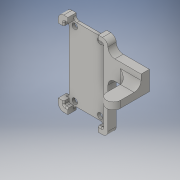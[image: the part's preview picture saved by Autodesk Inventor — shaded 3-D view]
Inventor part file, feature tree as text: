
AUTODESK INVENTOR PART (.ipt)
format: ipt  version: 2016 (Build 200138000, 138)  size: 251,392 bytes
history: native  units: in
note: dims shown in document units (in); Inventor stores cm internally (conversion verified against a paired STEP export)
features: fillet x5, extrude x4, sketch x3
ambient origin geometry x8: Origin, YZ Plane, XZ Plane, XY Plane, X Axis, Y Axis, Z Axis, Center Point
bodies: Solid1 (feature_tree)
feature tree (12):
  sketch  "Sketch1"  dims[d0=2.65in d1=1.4in]
  extrude  "Extrusion1"  Depth=1.4in
  extrude  "Extrusion2"  Depth=0.2in
  fillet  "Fillet1"  [1 undecoded]
  fillet  "Fillet2"  [1 undecoded]
  fillet  "Fillet3"  Radius=0.15in
  extrude  "Extrusion3"  Depth=0.7in
  fillet  "Fillet4"  Radius=1.325in
  extrude  "Extrusion4"  Depth=0.05in
  fillet  "Fillet5"  Radius=0.18in
  sketch  "Sketch2"  dims[d2=0.2in d3=0.2in d4=0.0in d5=0.0in d6=0.15in]
  sketch  "Sketch3"  dims[d7=0.15in d8=0.7in d9=1.325in d10=0.05in d11=0.18in d12=0.2in d13=0.2in d14=0.05in d15=0.1in d16=0.1in d17=0.0in d18=0.3in d19=0.0in d20=0.125in d21=0.05in d22=0.05in d23=0.7in d24=0.25in d25=1.2in d26=0.3in d27=0.0in d28=0.25in d29=0.25in d30=1.0in d31=0.5in d32=0.0in d33=0.25in]
note: 2 required parameter values undecoded (feature->parameter linkage not recoverable at this tier; creation-order binding heuristic only, values carry confidence <= 0.55)
